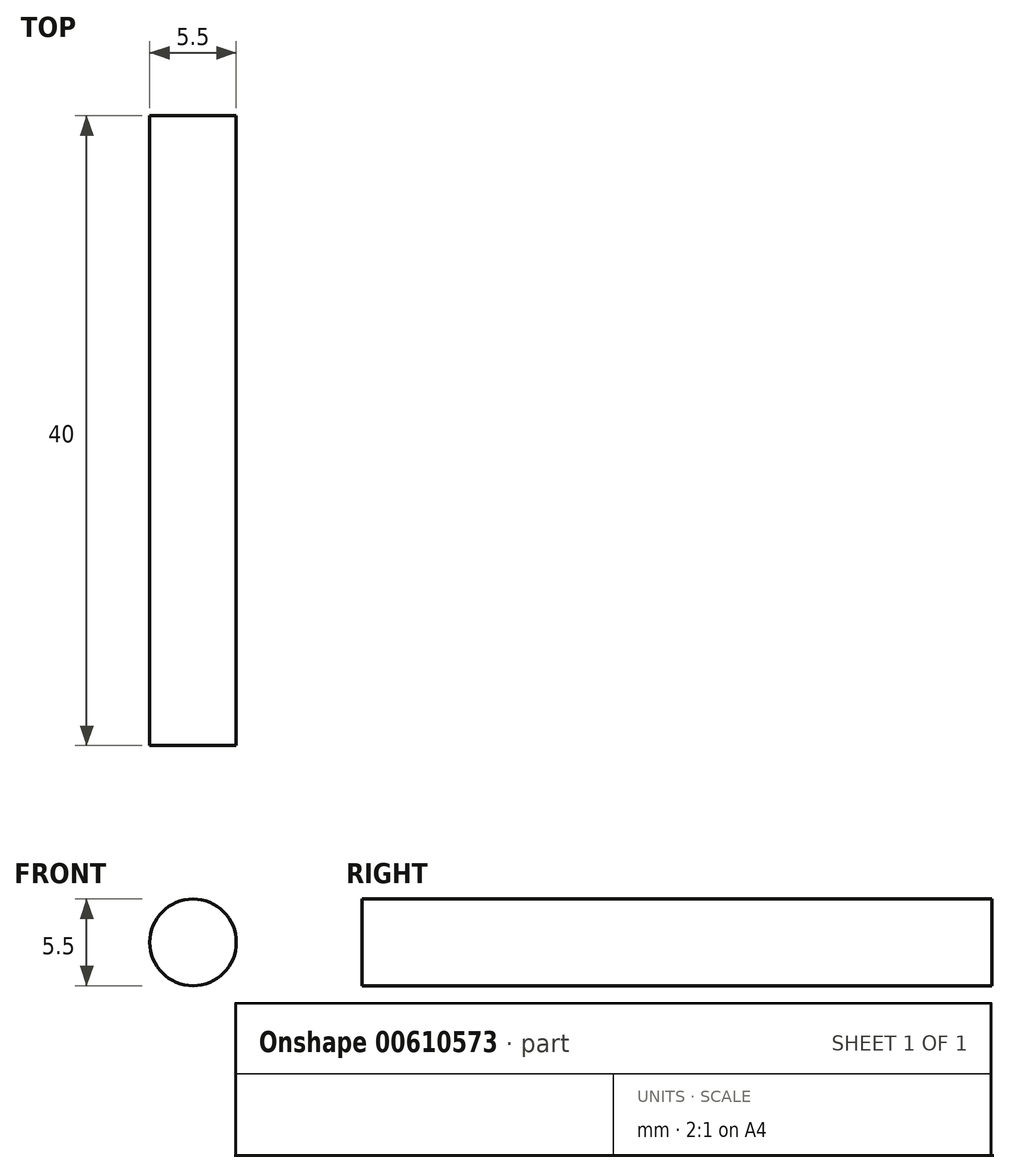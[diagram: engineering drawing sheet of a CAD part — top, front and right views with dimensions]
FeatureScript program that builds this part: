
annotation { "Feature Type Name" : "Feature", "Feature Type Description" : "" }
export const myFeature = defineFeature(function(context is Context, id is Id, definition is map)
    precondition{}
    {
        {
            var Q0;
            Q0=qCreatedBy(makeId("Front.planeOp"),FACE);
            var sketch = newSketch(context, id + "F0", { "sketchPlane" : qUnion([Q0])});
            skCircle(sketch, "E0", {"center": v(0, 0) * mm, "radius": 2.75 * mm});
            skSolve(sketch);
        }
        {
            var Q0;
            Q0=makeQuery(id+"F0.imprint","IMPRINT",FACE,{"disambiguationData":[TD([[makeQuery(id+"F0.imprint","IMPRINT",EDGE,{"derivedFrom":sQuery(id+"F0.wireOp",EDGE,"E0")}),1.0]])]});
            extrude(context, id + "F1", {"entities" : qUnion([Q0]), "depth" : 40 * mm, "offsetDistance" : 25.4 * mm});
        }
    });
